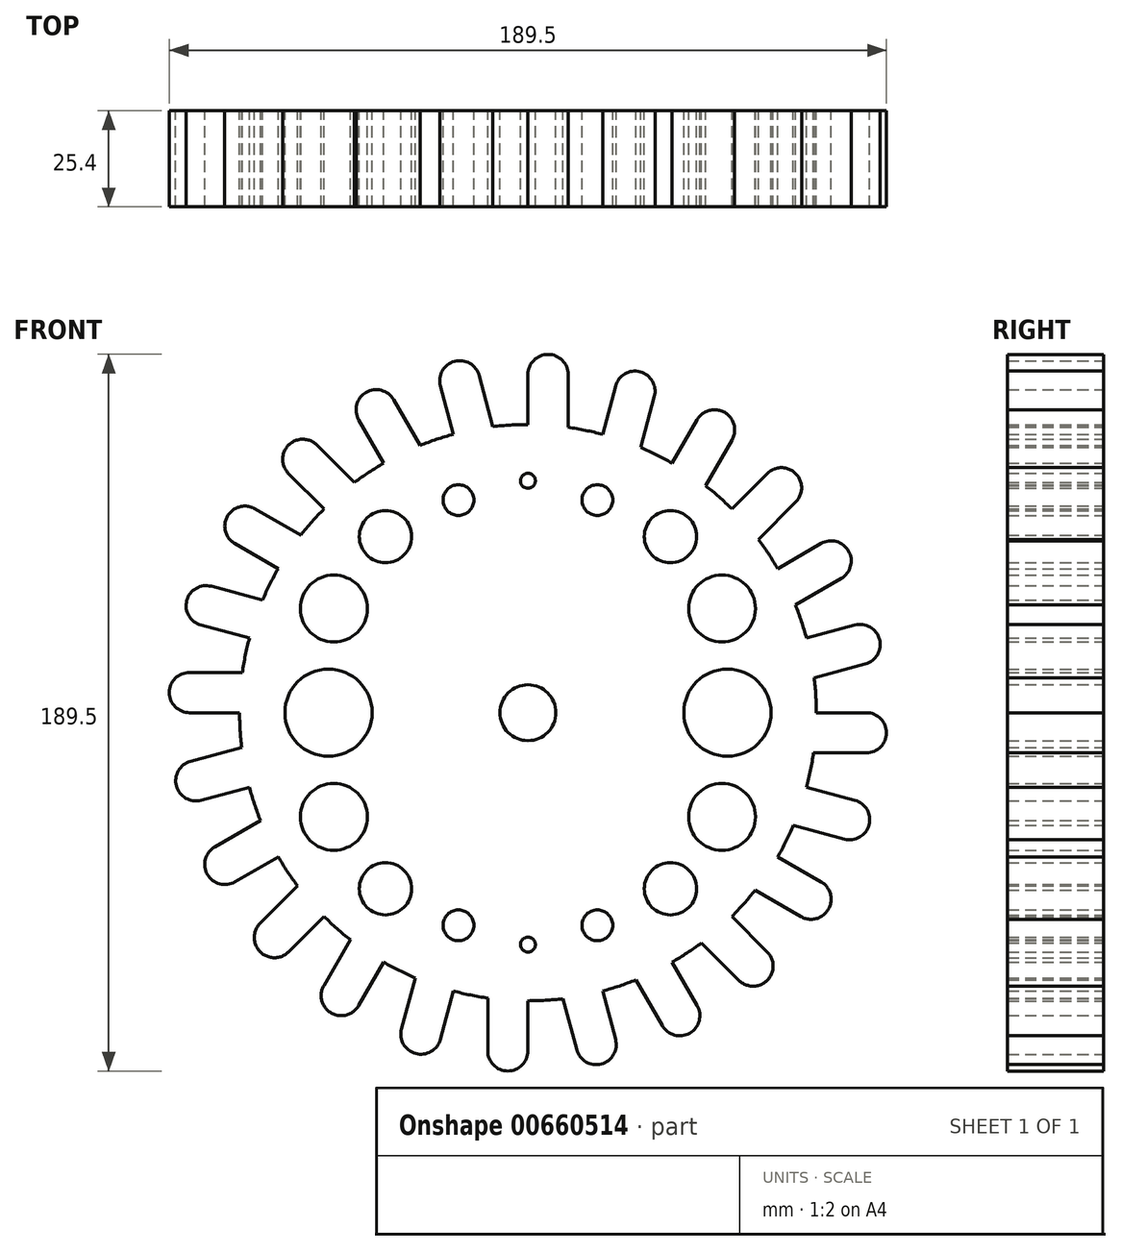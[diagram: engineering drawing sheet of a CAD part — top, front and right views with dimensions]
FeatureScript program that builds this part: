
annotation { "Feature Type Name" : "Feature", "Feature Type Description" : "" }
export const myFeature = defineFeature(function(context is Context, id is Id, definition is map)
    precondition{}
    {
        {
            var Q0;
            Q0=qCreatedBy(makeId("Front.planeOp"),FACE);
            var sketch = newSketch(context, id + "F0", { "sketchPlane" : qUnion([Q0])});
            skCircle(sketch, "E0", {"center": v(0, 0) * mm, "radius": 76.2 * mm});
            skLineSegment(sketch, "E1", {"start": v(0, 76.2) * mm, "end": v(0, 76.2) * mm});
            skLineSegment(sketch, "E2", {"start": v(0, 76.2) * mm, "end": v(0, 89.43) * mm});
            skLineSegment(sketch, "E3", {"start": v(10.63, 89.43) * mm, "end": v(10.63, 75.46) * mm});
            skLineSegment(sketch, "E4", {"start": v(-117.95, 0) * mm, "end": v(131.67, 0) * mm, "construction": true});
            skArc(sketch, "E5", {"start": v(0, 89.43) * mm, "mid": v(5.31, 94.75) * mm, "end": v(10.63, 89.43) * mm});
            skArc(sketch, "E6.1.0", {"start": v(-23.15, 86.39) * mm, "mid": v(-19.39, 92.9) * mm, "end": v(-12.88, 89.14) * mm});
            skLineSegment(sketch, "E6.1.1", {"start": v(-12.88, 89.14) * mm, "end": v(-9.26, 75.63) * mm});
            skLineSegment(sketch, "E6.1.2", {"start": v(-19.72, 73.6) * mm, "end": v(-23.15, 86.39) * mm});
            skArc(sketch, "E6.2.0", {"start": v(-44.72, 77.45) * mm, "mid": v(-42.77, 84.71) * mm, "end": v(-35.51, 82.77) * mm});
            skLineSegment(sketch, "E6.2.1", {"start": v(-35.51, 82.77) * mm, "end": v(-28.52, 70.66) * mm});
            skLineSegment(sketch, "E6.2.2", {"start": v(-38.1, 66) * mm, "end": v(-44.72, 77.45) * mm});
            skArc(sketch, "E6.3.0", {"start": v(-63.24, 63.24) * mm, "mid": v(-63.24, 70.75) * mm, "end": v(-55.72, 70.75) * mm});
            skLineSegment(sketch, "E6.3.1", {"start": v(-55.72, 70.75) * mm, "end": v(-45.84, 60.87) * mm});
            skLineSegment(sketch, "E6.3.2", {"start": v(-53.88, 53.88) * mm, "end": v(-63.24, 63.24) * mm});
            skArc(sketch, "E6.4.0", {"start": v(-77.45, 44.72) * mm, "mid": v(-79.4, 51.98) * mm, "end": v(-72.14, 53.92) * mm});
            skLineSegment(sketch, "E6.4.1", {"start": v(-72.14, 53.92) * mm, "end": v(-60.03, 46.93) * mm});
            skLineSegment(sketch, "E6.4.2", {"start": v(-66, 38.1) * mm, "end": v(-77.45, 44.72) * mm});
            skArc(sketch, "E6.5.0", {"start": v(-86.39, 23.15) * mm, "mid": v(-90.14, 29.66) * mm, "end": v(-83.64, 33.41) * mm});
            skLineSegment(sketch, "E6.5.1", {"start": v(-83.64, 33.41) * mm, "end": v(-70.13, 29.8) * mm});
            skLineSegment(sketch, "E6.5.2", {"start": v(-73.6, 19.72) * mm, "end": v(-86.39, 23.15) * mm});
            skArc(sketch, "E6.6.0", {"start": v(-89.43, 0) * mm, "mid": v(-94.75, 5.31) * mm, "end": v(-89.43, 10.63) * mm});
            skLineSegment(sketch, "E6.6.1", {"start": v(-89.43, 10.63) * mm, "end": v(-75.46, 10.63) * mm});
            skLineSegment(sketch, "E6.6.2", {"start": v(-76.2, 0) * mm, "end": v(-89.43, 0) * mm});
            skArc(sketch, "E6.7.0", {"start": v(-86.39, -23.15) * mm, "mid": v(-92.9, -19.39) * mm, "end": v(-89.14, -12.88) * mm});
            skLineSegment(sketch, "E6.7.1", {"start": v(-89.14, -12.88) * mm, "end": v(-75.63, -9.26) * mm});
            skLineSegment(sketch, "E6.7.2", {"start": v(-73.6, -19.72) * mm, "end": v(-86.39, -23.15) * mm});
            skArc(sketch, "E6.8.0", {"start": v(-77.45, -44.72) * mm, "mid": v(-84.71, -42.77) * mm, "end": v(-82.77, -35.51) * mm});
            skLineSegment(sketch, "E6.8.1", {"start": v(-82.77, -35.51) * mm, "end": v(-70.66, -28.52) * mm});
            skLineSegment(sketch, "E6.8.2", {"start": v(-66, -38.1) * mm, "end": v(-77.45, -44.72) * mm});
            skArc(sketch, "E6.9.0", {"start": v(-63.24, -63.24) * mm, "mid": v(-70.75, -63.24) * mm, "end": v(-70.75, -55.72) * mm});
            skLineSegment(sketch, "E6.9.1", {"start": v(-70.75, -55.72) * mm, "end": v(-60.87, -45.84) * mm});
            skLineSegment(sketch, "E6.9.2", {"start": v(-53.88, -53.88) * mm, "end": v(-63.24, -63.24) * mm});
            skArc(sketch, "E6.10.0", {"start": v(-44.72, -77.45) * mm, "mid": v(-51.98, -79.4) * mm, "end": v(-53.92, -72.14) * mm});
            skLineSegment(sketch, "E6.10.1", {"start": v(-53.92, -72.14) * mm, "end": v(-46.93, -60.03) * mm});
            skLineSegment(sketch, "E6.10.2", {"start": v(-38.1, -66) * mm, "end": v(-44.72, -77.45) * mm});
            skArc(sketch, "E6.11.0", {"start": v(-23.15, -86.39) * mm, "mid": v(-29.66, -90.14) * mm, "end": v(-33.41, -83.64) * mm});
            skLineSegment(sketch, "E6.11.1", {"start": v(-33.41, -83.64) * mm, "end": v(-29.8, -70.13) * mm});
            skLineSegment(sketch, "E6.11.2", {"start": v(-19.72, -73.6) * mm, "end": v(-23.15, -86.39) * mm});
            skArc(sketch, "E6.12.0", {"start": v(0, -89.43) * mm, "mid": v(-5.31, -94.75) * mm, "end": v(-10.63, -89.43) * mm});
            skLineSegment(sketch, "E6.12.1", {"start": v(-10.63, -89.43) * mm, "end": v(-10.63, -75.46) * mm});
            skLineSegment(sketch, "E6.12.2", {"start": v(0, -76.2) * mm, "end": v(0, -89.43) * mm});
            skArc(sketch, "E6.13.0", {"start": v(23.15, -86.39) * mm, "mid": v(19.39, -92.9) * mm, "end": v(12.88, -89.14) * mm});
            skLineSegment(sketch, "E6.13.1", {"start": v(12.88, -89.14) * mm, "end": v(9.26, -75.63) * mm});
            skLineSegment(sketch, "E6.13.2", {"start": v(19.72, -73.6) * mm, "end": v(23.15, -86.39) * mm});
            skArc(sketch, "E6.14.0", {"start": v(44.72, -77.45) * mm, "mid": v(42.77, -84.71) * mm, "end": v(35.51, -82.77) * mm});
            skLineSegment(sketch, "E6.14.1", {"start": v(35.51, -82.77) * mm, "end": v(28.52, -70.66) * mm});
            skLineSegment(sketch, "E6.14.2", {"start": v(38.1, -66) * mm, "end": v(44.72, -77.45) * mm});
            skArc(sketch, "E6.15.0", {"start": v(63.24, -63.24) * mm, "mid": v(63.24, -70.75) * mm, "end": v(55.72, -70.75) * mm});
            skLineSegment(sketch, "E6.15.1", {"start": v(55.72, -70.75) * mm, "end": v(45.84, -60.87) * mm});
            skLineSegment(sketch, "E6.15.2", {"start": v(53.88, -53.88) * mm, "end": v(63.24, -63.24) * mm});
            skArc(sketch, "E6.16.0", {"start": v(77.45, -44.72) * mm, "mid": v(79.4, -51.98) * mm, "end": v(72.14, -53.92) * mm});
            skLineSegment(sketch, "E6.16.1", {"start": v(72.14, -53.92) * mm, "end": v(60.03, -46.93) * mm});
            skLineSegment(sketch, "E6.16.2", {"start": v(66, -38.1) * mm, "end": v(77.45, -44.72) * mm});
            skArc(sketch, "E6.17.0", {"start": v(86.39, -23.15) * mm, "mid": v(90.14, -29.66) * mm, "end": v(83.64, -33.41) * mm});
            skLineSegment(sketch, "E6.17.1", {"start": v(83.64, -33.41) * mm, "end": v(70.13, -29.8) * mm});
            skLineSegment(sketch, "E6.17.2", {"start": v(73.6, -19.72) * mm, "end": v(86.39, -23.15) * mm});
            skArc(sketch, "E6.18.0", {"start": v(89.43, 0) * mm, "mid": v(94.75, -5.31) * mm, "end": v(89.43, -10.63) * mm});
            skLineSegment(sketch, "E6.18.1", {"start": v(89.43, -10.63) * mm, "end": v(75.46, -10.63) * mm});
            skLineSegment(sketch, "E6.18.2", {"start": v(76.2, 0) * mm, "end": v(89.43, 0) * mm});
            skArc(sketch, "E6.19.0", {"start": v(86.39, 23.15) * mm, "mid": v(92.9, 19.39) * mm, "end": v(89.14, 12.88) * mm});
            skLineSegment(sketch, "E6.19.1", {"start": v(89.14, 12.88) * mm, "end": v(75.63, 9.26) * mm});
            skLineSegment(sketch, "E6.19.2", {"start": v(73.6, 19.72) * mm, "end": v(86.39, 23.15) * mm});
            skArc(sketch, "E6.20.0", {"start": v(77.45, 44.72) * mm, "mid": v(84.71, 42.77) * mm, "end": v(82.77, 35.51) * mm});
            skLineSegment(sketch, "E6.20.1", {"start": v(82.77, 35.51) * mm, "end": v(70.66, 28.52) * mm});
            skLineSegment(sketch, "E6.20.2", {"start": v(66, 38.1) * mm, "end": v(77.45, 44.72) * mm});
            skArc(sketch, "E6.21.0", {"start": v(63.24, 63.24) * mm, "mid": v(70.75, 63.24) * mm, "end": v(70.75, 55.72) * mm});
            skLineSegment(sketch, "E6.21.1", {"start": v(70.75, 55.72) * mm, "end": v(60.87, 45.84) * mm});
            skLineSegment(sketch, "E6.21.2", {"start": v(53.88, 53.88) * mm, "end": v(63.24, 63.24) * mm});
            skArc(sketch, "E6.22.0", {"start": v(44.72, 77.45) * mm, "mid": v(51.98, 79.4) * mm, "end": v(53.92, 72.14) * mm});
            skLineSegment(sketch, "E6.22.1", {"start": v(53.92, 72.14) * mm, "end": v(46.93, 60.03) * mm});
            skLineSegment(sketch, "E6.22.2", {"start": v(38.1, 66) * mm, "end": v(44.72, 77.45) * mm});
            skArc(sketch, "E6.23.0", {"start": v(23.15, 86.39) * mm, "mid": v(29.66, 90.14) * mm, "end": v(33.41, 83.64) * mm});
            skLineSegment(sketch, "E6.23.1", {"start": v(33.41, 83.64) * mm, "end": v(29.8, 70.13) * mm});
            skLineSegment(sketch, "E6.23.2", {"start": v(19.72, 73.6) * mm, "end": v(23.15, 86.39) * mm});
            skCircle(sketch, "E7", {"center": v(0, 0) * mm, "radius": 7.4 * mm});
            skCircle(sketch, "E8", {"center": v(0, 61.32) * mm, "radius": 1.97 * mm});
            skCircle(sketch, "E9", {"center": v(18.36, 56.21) * mm, "radius": 4.06 * mm});
            skCircle(sketch, "E10", {"center": v(51.29, 27.54) * mm, "radius": 8.84 * mm});
            skCircle(sketch, "E11", {"center": v(37.66, 46.56) * mm, "radius": 6.9 * mm});
            skCircle(sketch, "E12", {"center": v(52.7, 0) * mm, "radius": 11.53 * mm});
            skLineSegment(sketch, "E13", {"start": v(0, 102.77) * mm, "end": v(0, -97.65) * mm, "construction": true});
            skCircle(sketch, "E14.MirrorC", {"center": v(-18.36, 56.21) * mm, "radius": 4.06 * mm});
            skCircle(sketch, "E15.MirrorC", {"center": v(-37.66, 46.56) * mm, "radius": 6.9 * mm});
            skCircle(sketch, "E16.MirrorC", {"center": v(-51.29, 27.54) * mm, "radius": 8.84 * mm});
            skCircle(sketch, "E17.MirrorC", {"center": v(-52.7, 0) * mm, "radius": 11.53 * mm});
            skCircle(sketch, "E18.MirrorC", {"center": v(18.36, -56.21) * mm, "radius": 4.06 * mm});
            skCircle(sketch, "E19.MirrorC", {"center": v(37.66, -46.56) * mm, "radius": 6.9 * mm});
            skCircle(sketch, "E20.MirrorC", {"center": v(51.29, -27.54) * mm, "radius": 8.84 * mm});
            skCircle(sketch, "E21.MirrorC", {"center": v(-37.66, -46.56) * mm, "radius": 6.9 * mm});
            skCircle(sketch, "E22.MirrorC", {"center": v(-51.29, -27.54) * mm, "radius": 8.84 * mm});
            skCircle(sketch, "E23.MirrorC", {"center": v(-18.36, -56.21) * mm, "radius": 4.06 * mm});
            skCircle(sketch, "E24.MirrorC", {"center": v(0, -61.32) * mm, "radius": 1.97 * mm});
            skSolve(sketch);
        }
        {
            var Q0;
            Q0 = qSketchRegion(id + "F0", true);
            extrude(context, id + "F1", {"entities" : qUnion([Q0]), "depth" : 25.4 * mm, "offsetDistance" : 25.4 * mm});
        }
    });
